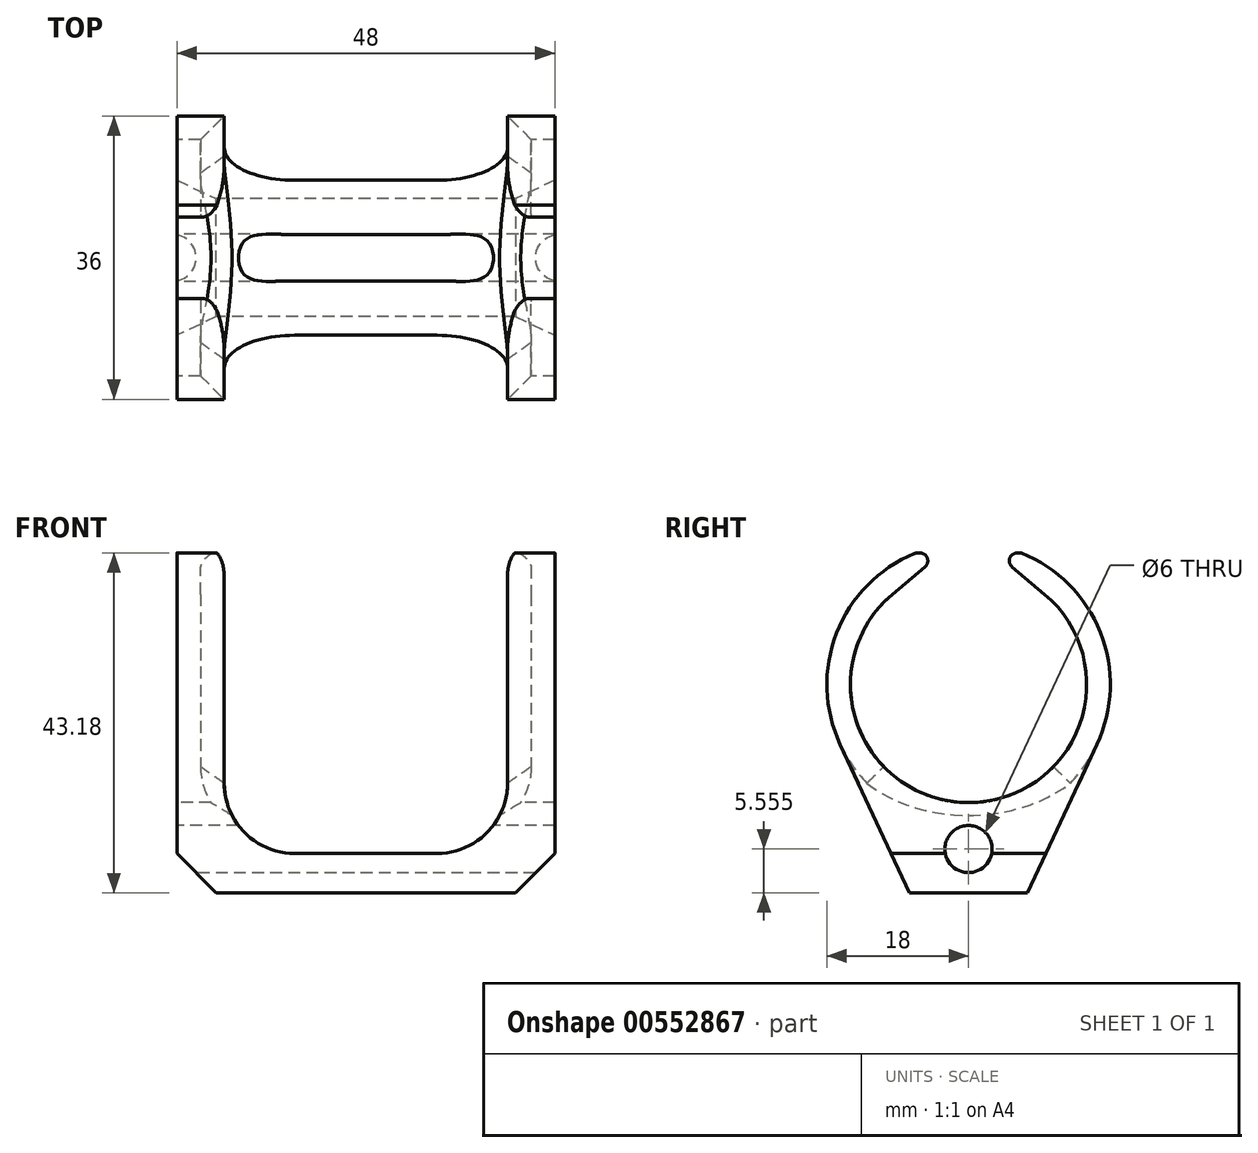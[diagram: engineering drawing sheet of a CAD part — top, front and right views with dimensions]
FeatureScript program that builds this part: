
annotation { "Feature Type Name" : "Feature", "Feature Type Description" : "" }
export const myFeature = defineFeature(function(context is Context, id is Id, definition is map)
    precondition{}
    {
        {
            var Q0;
            Q0=qCreatedBy(makeId("Right.planeOp"),FACE);
            var sketch = newSketch(context, id + "F0", { "sketchPlane" : qUnion([Q0])});
            skArc(sketch, "E0", {"start": v(-9.67, 37.93) * mm, "mid": v(0, 11.46) * mm, "end": v(9.67, 37.93) * mm});
            skArc(sketch, "E1", {"start": v(16.3, 18.84) * mm, "mid": v(16.74, 33.08) * mm, "end": v(6.68, 43.18) * mm});
            skLineSegment(sketch, "E2", {"start": v(-7.5, 0) * mm, "end": v(-16.3, 18.84) * mm});
            skLineSegment(sketch, "E3", {"start": v(7.5, 0) * mm, "end": v(16.3, 18.84) * mm});
            skLineSegment(sketch, "E4", {"start": v(-7.5, 0) * mm, "end": v(7.5, 0) * mm});
            skCircle(sketch, "E5", {"center": v(0, 5.55) * mm, "radius": 3 * mm});
            skLineSegment(sketch, "E6", {"start": v(-3.44, 43.18) * mm, "end": v(-9.67, 37.93) * mm});
            skLineSegment(sketch, "E7", {"start": v(-9.67, 37.93) * mm, "end": v(-3.44, 43.18) * mm});
            skLineSegment(sketch, "E8", {"start": v(9.67, 37.93) * mm, "end": v(3.44, 43.18) * mm});
            skLineSegment(sketch, "E9", {"start": v(-6.68, 43.18) * mm, "end": v(-3.44, 43.18) * mm});
            skLineSegment(sketch, "E10.trimOffspring", {"start": v(3.44, 43.18) * mm, "end": v(6.68, 43.18) * mm});
            skArc(sketch, "E11.trimOffspring", {"start": v(-6.68, 43.18) * mm, "mid": v(-16.74, 33.08) * mm, "end": v(-16.3, 18.84) * mm});
            skPoint(sketch, "E12.orphan", {"position": v(0, 46.08) * mm});
            skSolve(sketch);
        }
        {
            var Q0;
            Q0=makeQuery(id+"F0.imprint","IMPRINT",FACE,{"disambiguationData":[TD([[makeQuery(id+"F0.imprint","IMPRINT",EDGE,{"derivedFrom":sQuery(id+"F0.wireOp",EDGE,"E0")}),-1.0]])]});
            extrude(context, id + "F1", {"entities" : qUnion([Q0]), "depth" : 30 * mm, "offsetDistance" : 25 * mm});
        }
        {
            var Q0;
            Q0=qSketchRegion(id+"F0",true);
            extrude(context, id + "F2", {"entities" : qUnion([Q0]), "operationType" : NewBodyOperationType.ADD, "oppositeDirection" : true, "depth" : 30 * mm, "offsetDistance" : 25 * mm});
        }
        {
            var Q0;
            Q0=qCreatedBy(makeId("Front.planeOp"),FACE);
            var sketch = newSketch(context, id + "F3", { "sketchPlane" : qUnion([Q0])});
            skLineSegment(sketch, "E13.bottom", {"start": v(-18, 45) * mm, "end": v(18, 45) * mm});
            skLineSegment(sketch, "E13.top", {"start": v(-18, 5) * mm, "end": v(18, 5) * mm});
            skLineSegment(sketch, "E13.left", {"start": v(-24, 45) * mm, "end": v(-24, 5) * mm});
            skLineSegment(sketch, "E13.right", {"start": v(24, 45) * mm, "end": v(24, 5) * mm});
            skLineSegment(sketch, "E14.left", {"start": v(-18, 45) * mm, "end": v(-18, 5) * mm});
            skLineSegment(sketch, "E14.right", {"start": v(18, 45) * mm, "end": v(18, 5) * mm});
            skLineSegment(sketch, "E15", {"start": v(-24, 45) * mm, "end": v(-38.05, 50.2) * mm});
            skLineSegment(sketch, "E16", {"start": v(-38.05, 50.2) * mm, "end": v(-38.05, -3.86) * mm});
            skLineSegment(sketch, "E17", {"start": v(-38.05, -3.86) * mm, "end": v(-24, -5.02) * mm});
            skLineSegment(sketch, "E18", {"start": v(-24, -5.02) * mm, "end": v(-24, 5) * mm});
            skLineSegment(sketch, "E19", {"start": v(24, 5) * mm, "end": v(24, -7.34) * mm});
            skLineSegment(sketch, "E20", {"start": v(24, -7.34) * mm, "end": v(42.2, -3.73) * mm});
            skLineSegment(sketch, "E21", {"start": v(42.2, -3.73) * mm, "end": v(42.2, 48.53) * mm});
            skLineSegment(sketch, "E22", {"start": v(42.2, 48.53) * mm, "end": v(24, 45) * mm});
            skSolve(sketch);
        }
        {
            var Q0;
            Q0=qSketchRegion(id+"F3",true);
            extrude(context, id + "F4", {"entities" : qUnion([Q0]), "operationType" : NewBodyOperationType.REMOVE, "endBound" : BoundingType.SYMMETRIC, "depth" : 36.6 * mm, "offsetDistance" : 25 * mm});
        }
        {
            var Q0;
            {var subQ1=sQuery(id+"F0.wireOp",EDGE,"E2");var subQ2=sQuery(id+"F3.wireOp",EDGE,"E14.left");var subQ3=sQuery(id+"F3.wireOp",EDGE,"E13.top");Q0=makeQuery(id+"F4.boolean.opBoolean","COPY",EDGE,{"disambiguationData":[TD([makeQuery(id+"F1.opExtrude","SWEPT_FACE",FACE,{"disambiguationData":[OSD([subQ1])]})])],"derivedFrom":makeQuery(id+"F4.opExtrude","SWEPT_EDGE",EDGE,{"disambiguationData":[OSD([subQ3,subQ2])]})});}
            var Q1;
            {var subQ1=sQuery(id+"F0.wireOp",EDGE,"E2");var subQ2=sQuery(id+"F3.wireOp",EDGE,"E13.top");var subQ3=sQuery(id+"F3.wireOp",EDGE,"E14.right");Q1=makeQuery(id+"F4.boolean.opBoolean","COPY",EDGE,{"disambiguationData":[TD([makeQuery(id+"F1.opExtrude","SWEPT_FACE",FACE,{"disambiguationData":[OSD([subQ1])]})])],"derivedFrom":makeQuery(id+"F4.opExtrude","SWEPT_EDGE",EDGE,{"disambiguationData":[OSD([subQ2,subQ3])]})});}
            fillet(context, id + "F5", {"entities" : qUnion([Q0, Q1]), "radius" : 8.93 * mm, "tangentPropagation" : true, "allowEdgeOverflow" : false});
        }
        {
            var Q0;
            {var subQ0=sQuery(id+"F0.wireOp",EDGE,"E0");Q0=makeQuery(id+"F4.boolean.opBoolean","INTERSECT",EDGE,{"derivedFrom":[makeQuery(id+"F2.boolean.opBoolean","MERGE",FACE,{"derivedFrom":[makeQuery(id+"F1.opExtrude","SWEPT_FACE",FACE,{"disambiguationData":[OSD([subQ0])]}),makeQuery(id+"F2.opExtrude","SWEPT_FACE",FACE,{"disambiguationData":[OSD([subQ0])]})]}),makeQuery(id+"F4.opExtrude","SWEPT_FACE",FACE,{"disambiguationData":[OSD([sQuery(id+"F3.wireOp",EDGE,"E14.right")])]})]});}
            var Q1;
            {var subQ0=sQuery(id+"F0.wireOp",EDGE,"E0");Q1=makeQuery(id+"F4.boolean.opBoolean","INTERSECT",EDGE,{"derivedFrom":[makeQuery(id+"F2.boolean.opBoolean","MERGE",FACE,{"derivedFrom":[makeQuery(id+"F1.opExtrude","SWEPT_FACE",FACE,{"disambiguationData":[OSD([subQ0])]}),makeQuery(id+"F2.opExtrude","SWEPT_FACE",FACE,{"disambiguationData":[OSD([subQ0])]})]}),makeQuery(id+"F4.opExtrude","SWEPT_FACE",FACE,{"disambiguationData":[OSD([sQuery(id+"F3.wireOp",EDGE,"E14.left")])]})]});}
            chamfer(context, id + "F6", {"entities" : qUnion([Q0, Q1]), "width" : 3 * mm, "tangentPropagation" : true});
        }
        {
            var Q0;
            {var subQ0=sQuery(id+"F0.wireOp",EDGE,"E4");Q0=makeQuery(id+"F4.boolean.opBoolean","INTERSECT",EDGE,{"derivedFrom":[makeQuery(id+"F2.boolean.opBoolean","MERGE",FACE,{"derivedFrom":[makeQuery(id+"F1.opExtrude","SWEPT_FACE",FACE,{"disambiguationData":[OSD([subQ0])]}),makeQuery(id+"F2.opExtrude","SWEPT_FACE",FACE,{"disambiguationData":[OSD([subQ0])]})]}),makeQuery(id+"F4.opExtrude","SWEPT_FACE",FACE,{"disambiguationData":[OSD([sQuery(id+"F3.wireOp",EDGE,"E13.left"),sQuery(id+"F3.wireOp",EDGE,"E18")])]})]});}
            var Q1;
            {var subQ0=sQuery(id+"F0.wireOp",EDGE,"E4");Q1=makeQuery(id+"F4.boolean.opBoolean","INTERSECT",EDGE,{"derivedFrom":[makeQuery(id+"F2.boolean.opBoolean","MERGE",FACE,{"derivedFrom":[makeQuery(id+"F1.opExtrude","SWEPT_FACE",FACE,{"disambiguationData":[OSD([subQ0])]}),makeQuery(id+"F2.opExtrude","SWEPT_FACE",FACE,{"disambiguationData":[OSD([subQ0])]})]}),makeQuery(id+"F4.opExtrude","SWEPT_FACE",FACE,{"disambiguationData":[OSD([sQuery(id+"F3.wireOp",EDGE,"E13.right"),sQuery(id+"F3.wireOp",EDGE,"E19")])]})]});}
            chamfer(context, id + "F7", {"entities" : qUnion([Q0, Q1]), "width" : 5 * mm, "tangentPropagation" : true});
        }
        {
            var Q0;
            {var subQ0=sQuery(id+"F0.wireOp",EDGE,"E10.trimOffspring");var subQ1=sQuery(id+"F0.wireOp",EDGE,"E8");Q0=makeQuery(id+"F4.boolean.opBoolean","SPLIT",EDGE,{"disambiguationData":[TD([makeQuery(id+"F4.opExtrude","SWEPT_FACE",FACE,{"disambiguationData":[OSD([sQuery(id+"F3.wireOp",EDGE,"E14.right")])]})])],"derivedFrom":makeQuery(id+"F2.boolean.opBoolean","MERGE",EDGE,{"derivedFrom":[makeQuery(id+"F1.opExtrude","SWEPT_EDGE",EDGE,{"disambiguationData":[OSD([subQ1,subQ0])]}),makeQuery(id+"F2.opExtrude","SWEPT_EDGE",EDGE,{"disambiguationData":[OSD([subQ1,subQ0])]})]})});}
            var Q1;
            {var subQ0=sQuery(id+"F0.wireOp",EDGE,"E9");var subQ1=sQuery(id+"F0.wireOp",EDGE,"E7");Q1=makeQuery(id+"F4.boolean.opBoolean","SPLIT",EDGE,{"disambiguationData":[TD([makeQuery(id+"F4.opExtrude","SWEPT_FACE",FACE,{"disambiguationData":[OSD([sQuery(id+"F3.wireOp",EDGE,"E14.right")])]})])],"derivedFrom":makeQuery(id+"F2.boolean.opBoolean","MERGE",EDGE,{"derivedFrom":[makeQuery(id+"F1.opExtrude","SWEPT_EDGE",EDGE,{"disambiguationData":[OSD([subQ1,subQ0])]}),makeQuery(id+"F2.opExtrude","SWEPT_EDGE",EDGE,{"disambiguationData":[OSD([subQ1,subQ0])]})]})});}
            var Q2;
            {var subQ0=sQuery(id+"F0.wireOp",EDGE,"E9");var subQ1=sQuery(id+"F0.wireOp",EDGE,"E7");Q2=makeQuery(id+"F4.boolean.opBoolean","SPLIT",EDGE,{"disambiguationData":[TD([makeQuery(id+"F4.opExtrude","SWEPT_FACE",FACE,{"disambiguationData":[OSD([sQuery(id+"F3.wireOp",EDGE,"E14.left")])]})])],"derivedFrom":makeQuery(id+"F2.boolean.opBoolean","MERGE",EDGE,{"derivedFrom":[makeQuery(id+"F1.opExtrude","SWEPT_EDGE",EDGE,{"disambiguationData":[OSD([subQ1,subQ0])]}),makeQuery(id+"F2.opExtrude","SWEPT_EDGE",EDGE,{"disambiguationData":[OSD([subQ1,subQ0])]})]})});}
            var Q3;
            {var subQ0=sQuery(id+"F0.wireOp",EDGE,"E10.trimOffspring");var subQ1=sQuery(id+"F0.wireOp",EDGE,"E8");Q3=makeQuery(id+"F4.boolean.opBoolean","SPLIT",EDGE,{"disambiguationData":[TD([makeQuery(id+"F4.opExtrude","SWEPT_FACE",FACE,{"disambiguationData":[OSD([sQuery(id+"F3.wireOp",EDGE,"E14.left")])]})])],"derivedFrom":makeQuery(id+"F2.boolean.opBoolean","MERGE",EDGE,{"derivedFrom":[makeQuery(id+"F1.opExtrude","SWEPT_EDGE",EDGE,{"disambiguationData":[OSD([subQ1,subQ0])]}),makeQuery(id+"F2.opExtrude","SWEPT_EDGE",EDGE,{"disambiguationData":[OSD([subQ1,subQ0])]})]})});}
            fillet(context, id + "F8", {"entities" : qUnion([Q0, Q1, Q2, Q3]), "radius" : 1 * mm, "tangentPropagation" : true, "allowEdgeOverflow" : false});
        }
    });
